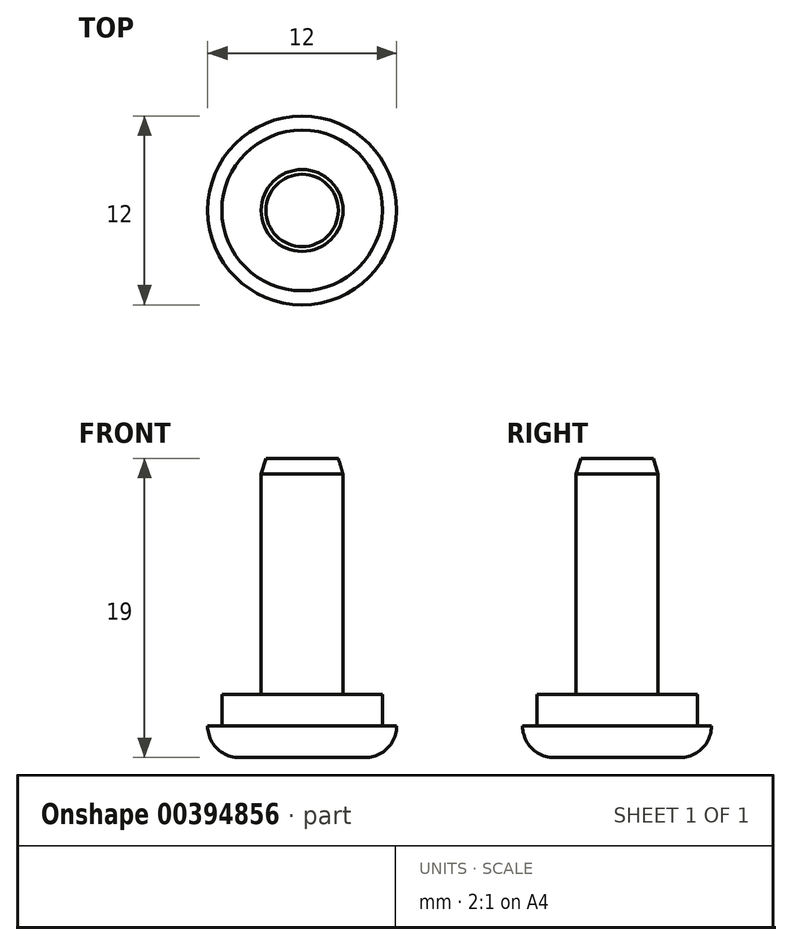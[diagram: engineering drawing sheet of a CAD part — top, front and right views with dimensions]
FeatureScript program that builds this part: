
annotation { "Feature Type Name" : "Feature", "Feature Type Description" : "" }
export const myFeature = defineFeature(function(context is Context, id is Id, definition is map)
    precondition{}
    {
        {
            var Q0;
            Q0=qCreatedBy(makeId("Front.planeOp"),FACE);
            var sketch = newSketch(context, id + "F0", { "sketchPlane" : qUnion([Q0])});
            skLineSegment(sketch, "E0", {"start": v(5.1, 2) * mm, "end": v(5.1, 4) * mm});
            skLineSegment(sketch, "E1", {"start": v(5.1, 2) * mm, "end": v(6, 2) * mm});
            skLineSegment(sketch, "E2", {"start": v(5.1, 4) * mm, "end": v(2.6, 4) * mm});
            skLineSegment(sketch, "E3", {"start": v(0, 14) * mm, "end": v(0, 0) * mm});
            skLineSegment(sketch, "E4", {"start": v(0, 0) * mm, "end": v(4, 0) * mm});
            skLineSegment(sketch, "E5", {"start": v(6, 2) * mm, "end": v(6, 2) * mm});
            skLineSegment(sketch, "E6", {"start": v(2.6, 18) * mm, "end": v(2.3, 19) * mm});
            skLineSegment(sketch, "E7", {"start": v(2.3, 19) * mm, "end": v(0, 19) * mm});
            skLineSegment(sketch, "E8", {"start": v(0, 19) * mm, "end": v(0, 14) * mm});
            skLineSegment(sketch, "E9", {"start": v(2.6, 18) * mm, "end": v(2.6, 4) * mm});
            skPoint(sketch, "E10.visualSharp", {"position": v(6, 0) * mm});
            skArc(sketch, "E10.filletArc", {"start": v(4, 0) * mm, "mid": v(5.41, 0.59) * mm, "end": v(6, 2) * mm});
            skSolve(sketch);
        }
        {
            var Q0;
            Q0 = qSketchRegion(id + "F0", true);
            var Q1;
            Q1=sQuery(id+"F0.wireOp",EDGE,"E3");
            revolve(context, id + "F1", {"entities" : qUnion([Q0]), "axis" : qUnion([Q1]), "revolveType" : RevolveType.FULL});
        }
    });
